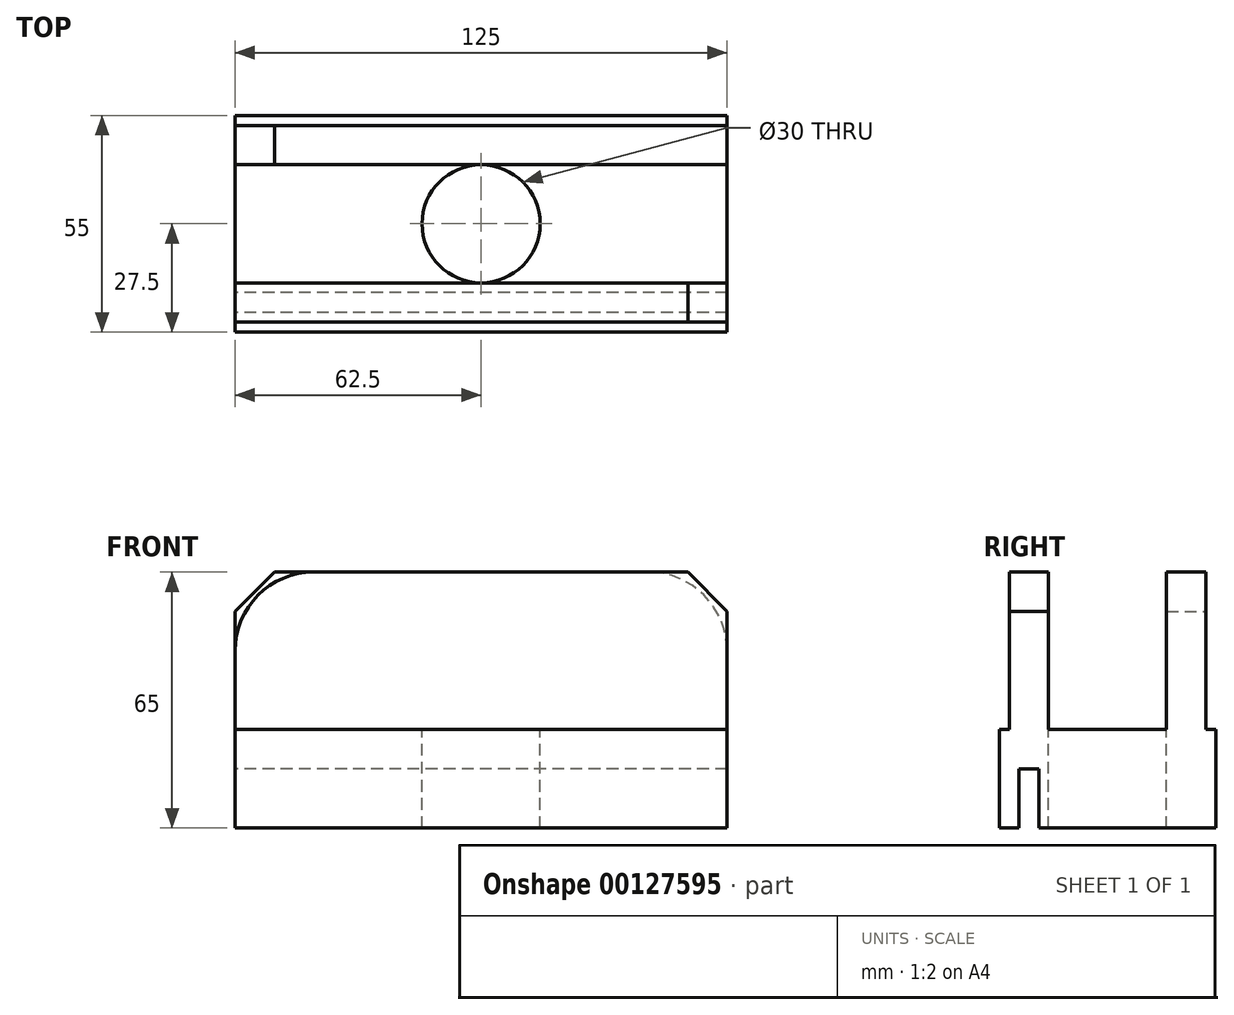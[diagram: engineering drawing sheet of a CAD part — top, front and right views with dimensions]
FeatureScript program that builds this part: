
annotation { "Feature Type Name" : "Feature", "Feature Type Description" : "" }
export const myFeature = defineFeature(function(context is Context, id is Id, definition is map)
    precondition{}
    {
        {
            var Q0;
            Q0=qCreatedBy(makeId("Front.planeOp"),FACE);
            var sketch = newSketch(context, id + "F0", { "sketchPlane" : qUnion([Q0])});
            skLineSegment(sketch, "E0.bottom", {"start": v(-62.5, 12.5) * mm, "end": v(62.5, 12.5) * mm});
            skLineSegment(sketch, "E0.top", {"start": v(-62.5, -12.5) * mm, "end": v(62.5, -12.5) * mm});
            skLineSegment(sketch, "E0.left", {"start": v(-62.5, 12.5) * mm, "end": v(-62.5, -12.5) * mm});
            skLineSegment(sketch, "E0.right", {"start": v(62.5, 12.5) * mm, "end": v(62.5, -12.5) * mm});
            skPoint(sketch, "E0.middle", {"position": v(0, 0) * mm});
            skSolve(sketch);
        }
        {
            var Q0;
            Q0 = qSketchRegion(id + "F0", true);
            extrude(context, id + "F1", {"entities" : qUnion([Q0]), "depth" : 55 * mm});
        }
        {
            var Q0;
            Q0=makeQuery(id+"F1.opExtrude","SWEPT_FACE",FACE,{"disambiguationData":[OSD([sQuery(id+"F0.wireOp",EDGE,"E0.left")])]});
            var sketch = newSketch(context, id + "F2", { "sketchPlane" : qUnion([Q0])});
            skLineSegment(sketch, "E1.bottom", {"start": v(45, 2.5) * mm, "end": v(50, 2.5) * mm});
            skLineSegment(sketch, "E1.top", {"start": v(45, -27.5) * mm, "end": v(50, -27.5) * mm});
            skLineSegment(sketch, "E1.left", {"start": v(45, 2.5) * mm, "end": v(45, -27.5) * mm});
            skLineSegment(sketch, "E1.right", {"start": v(50, 2.5) * mm, "end": v(50, -27.5) * mm});
            skPoint(sketch, "E1.middle", {"position": v(47.5, -12.5) * mm});
            skSolve(sketch);
        }
        {
            var Q0;
            Q0 = qSketchRegion(id + "F2", true);
            extrude(context, id + "F3", {"entities" : qUnion([Q0]), "operationType" : NewBodyOperationType.REMOVE, "endBound" : BoundingType.THROUGH_ALL, "oppositeDirection" : true, "depth" : 25 * mm});
        }
        {
            var Q0;
            Q0=makeQuery(id+"F1.opExtrude","SWEPT_FACE",FACE,{"disambiguationData":[OSD([sQuery(id+"F0.wireOp",EDGE,"E0.bottom")])]});
            var sketch = newSketch(context, id + "F4", { "sketchPlane" : qUnion([Q0])});
            skLineSegment(sketch, "E2.bottom", {"start": v(-62.5, -52.5) * mm, "end": v(62.5, -52.5) * mm});
            skLineSegment(sketch, "E2.top", {"start": v(-62.5, -42.5) * mm, "end": v(62.5, -42.5) * mm});
            skLineSegment(sketch, "E2.left", {"start": v(-62.5, -52.5) * mm, "end": v(-62.5, -42.5) * mm});
            skLineSegment(sketch, "E2.right", {"start": v(62.5, -52.5) * mm, "end": v(62.5, -42.5) * mm});
            skLineSegment(sketch, "E3.bottom", {"start": v(-62.5, -2.5) * mm, "end": v(62.5, -2.5) * mm});
            skLineSegment(sketch, "E3.top", {"start": v(-62.5, -12.5) * mm, "end": v(62.5, -12.5) * mm});
            skLineSegment(sketch, "E3.left", {"start": v(-62.5, -2.5) * mm, "end": v(-62.5, -12.5) * mm});
            skLineSegment(sketch, "E3.right", {"start": v(62.5, -2.5) * mm, "end": v(62.5, -12.5) * mm});
            skPoint(sketch, "E4", {"position": v(0, -27.5) * mm});
            skPoint(sketch, "E4.positionSnap0", {"position": v(-62.5, -27.5) * mm});
            skPoint(sketch, "E4.positionSnap1", {"position": v(0, 0) * mm});
            skSolve(sketch);
        }
        {
            var Q0;
            Q0 = qSketchRegion(id + "F4", true);
            extrude(context, id + "F5", {"entities" : qUnion([Q0]), "operationType" : NewBodyOperationType.ADD, "depth" : 40 * mm});
        }
        {
            var Q0;
            Q0=makeQuery(id+"F5.opExtrude","CAP_EDGE",EDGE,{"disambiguationData":[OSD([sQuery(id+"F4.wireOp",EDGE,"E2.left")])],"isStart":false});
            fillet(context, id + "F6", {"entities" : qUnion([Q0]), "radius" : 20 * mm, "tangentPropagation" : true, "allowEdgeOverflow" : false});
        }
        {
            var Q0;
            Q0=makeQuery(id+"F5.opExtrude","CAP_EDGE",EDGE,{"disambiguationData":[OSD([sQuery(id+"F4.wireOp",EDGE,"E3.right")])],"isStart":false});
            fillet(context, id + "F7", {"entities" : qUnion([Q0]), "radius" : 20 * mm, "tangentPropagation" : true, "allowEdgeOverflow" : false});
        }
        {
            var Q0;
            Q0=makeQuery(id+"F5.opExtrude","CAP_EDGE",EDGE,{"disambiguationData":[OSD([sQuery(id+"F4.wireOp",EDGE,"E2.right")])],"isStart":false});
            chamfer(context, id + "F8", {"entities" : qUnion([Q0]), "width" : 10 * mm, "tangentPropagation" : true});
        }
        {
            var Q0;
            Q0=makeQuery(id+"F5.opExtrude","CAP_EDGE",EDGE,{"disambiguationData":[OSD([sQuery(id+"F4.wireOp",EDGE,"E3.left")])],"isStart":false});
            chamfer(context, id + "F9", {"entities" : qUnion([Q0]), "width" : 10 * mm, "tangentPropagation" : true});
        }
        {
            var Q0;
            Q0=makeQuery(id+"F5.boolean.opBoolean","SPLIT",FACE,{"disambiguationData":[TD([makeQuery(id+"F5.opExtrude","SWEPT_FACE",FACE,{"disambiguationData":[OSD([sQuery(id+"F4.wireOp",EDGE,"E2.top")])]})])],"derivedFrom":makeQuery(id+"F1.opExtrude","SWEPT_FACE",FACE,{"disambiguationData":[OSD([sQuery(id+"F0.wireOp",EDGE,"E0.bottom")])]})});
            var sketch = newSketch(context, id + "F10", { "sketchPlane" : qUnion([Q0])});
            skCircle(sketch, "E5", {"center": v(0, -27.5) * mm, "radius": 15 * mm});
            skPoint(sketch, "E5.centerSnap0", {"position": v(62.5, -27.5) * mm});
            skSolve(sketch);
        }
        {
            var Q0;
            Q0 = qSketchRegion(id + "F10", true);
            extrude(context, id + "F11", {"entities" : qUnion([Q0]), "operationType" : NewBodyOperationType.REMOVE, "endBound" : BoundingType.THROUGH_ALL, "oppositeDirection" : true, "depth" : 25 * mm});
        }
    });
